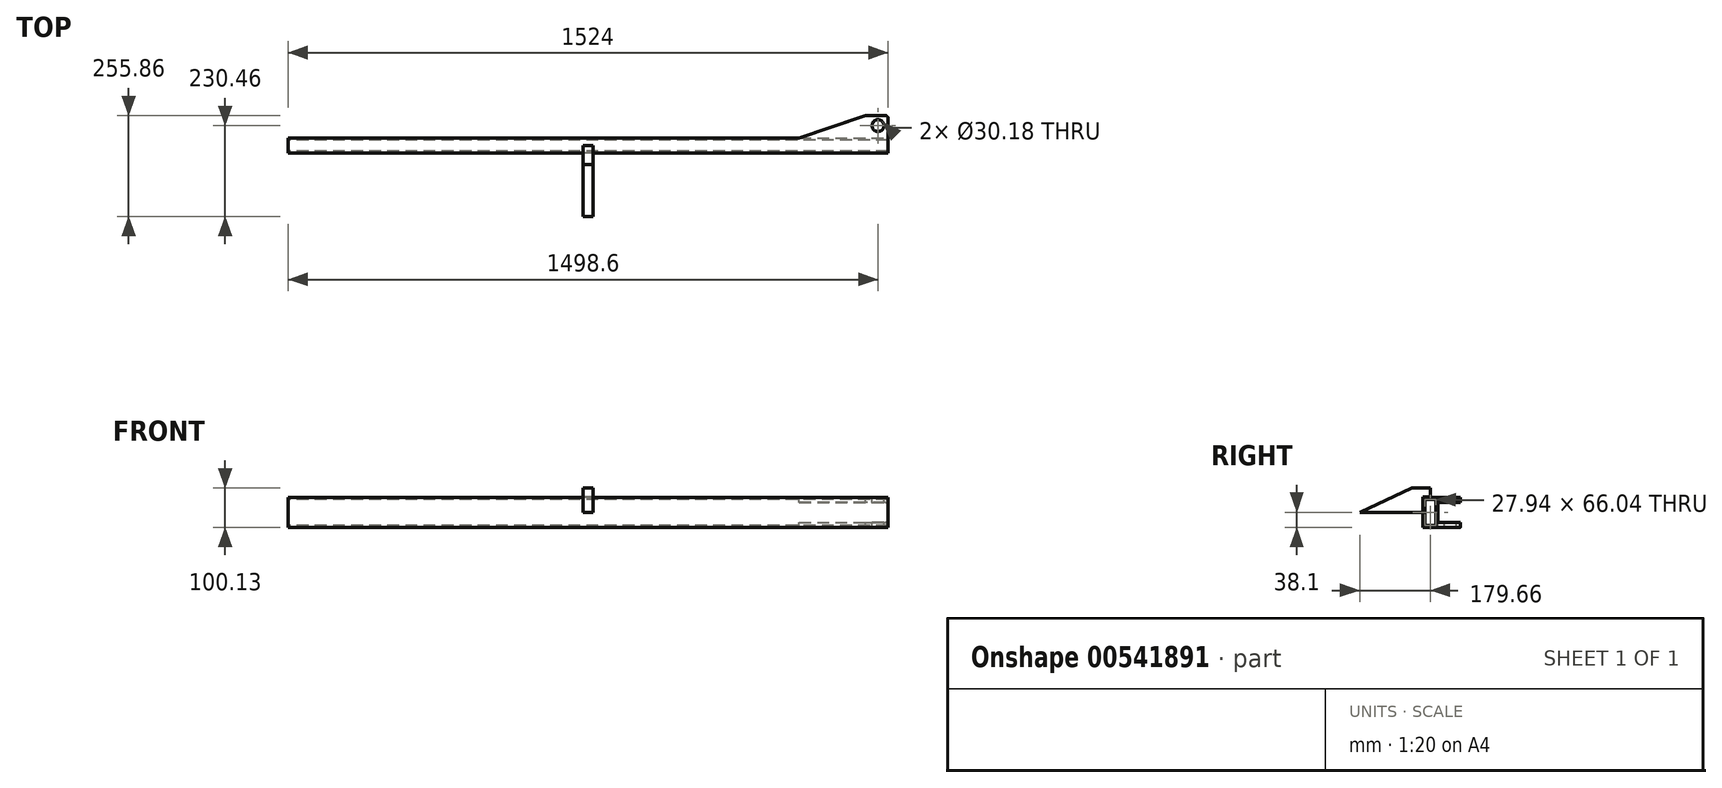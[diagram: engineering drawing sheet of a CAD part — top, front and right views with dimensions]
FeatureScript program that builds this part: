
annotation { "Feature Type Name" : "Feature", "Feature Type Description" : "" }
export const myFeature = defineFeature(function(context is Context, id is Id, definition is map)
    precondition{}
    {
        {
            var Q0;
            Q0=qCreatedBy(makeId("Right.planeOp"),FACE);
            var sketch = newSketch(context, id + "F0", { "sketchPlane" : qUnion([Q0])});
            skLineSegment(sketch, "E0.bottom", {"start": v(-19.05, 38.1) * mm, "end": v(19.05, 38.1) * mm});
            skLineSegment(sketch, "E0.top", {"start": v(-19.05, -38.1) * mm, "end": v(19.05, -38.1) * mm});
            skLineSegment(sketch, "E0.left", {"start": v(-19.05, 38.1) * mm, "end": v(-19.05, -38.1) * mm});
            skLineSegment(sketch, "E0.right", {"start": v(19.05, 38.1) * mm, "end": v(19.05, -38.1) * mm});
            skPoint(sketch, "E0.middle", {"position": v(0, 0) * mm});
            skSolve(sketch);
        }
        {
            var Q0;
            Q0 = qSketchRegion(id + "F0", true);
            extrude(context, id + "F1", {"entities" : qUnion([Q0]), "endBound" : BoundingType.SYMMETRIC, "depth" : 1524 * mm, "offsetDistance" : 25.4 * mm});
        }
        {
            var Q0;
            Q0=makeQuery(id+"F1.opExtrude","CAP_FACE",FACE,{"disambiguationData":[OSD([sQuery(id+"F0.wireOp",EDGE,"E0.bottom"),sQuery(id+"F0.wireOp",EDGE,"E0.top"),sQuery(id+"F0.wireOp",EDGE,"E0.left"),sQuery(id+"F0.wireOp",EDGE,"E0.right")])],"isStart":true});
            var Q1;
            Q1=makeQuery(id+"F1.opExtrude","CAP_FACE",FACE,{"disambiguationData":[OSD([sQuery(id+"F0.wireOp",EDGE,"E0.bottom"),sQuery(id+"F0.wireOp",EDGE,"E0.top"),sQuery(id+"F0.wireOp",EDGE,"E0.left"),sQuery(id+"F0.wireOp",EDGE,"E0.right")])],"isStart":false});
            shell(context, id + "F2", {"entities" : qUnion([Q0, Q1]), "thickness" : 5.08 * mm});
        }
        {
            var Q0;
            Q0=makeQuery(id+"F1.opExtrude","SWEPT_FACE",FACE,{"disambiguationData":[OSD([sQuery(id+"F0.wireOp",EDGE,"E0.bottom")])]});
            var sketch = newSketch(context, id + "F3", { "sketchPlane" : qUnion([Q0])});
            skLineSegment(sketch, "E1", {"start": v(762, 19.05) * mm, "end": v(762, 69.85) * mm});
            skLineSegment(sketch, "E2", {"start": v(755.65, 76.2) * mm, "end": v(704.85, 76.2) * mm});
            skLineSegment(sketch, "E3", {"start": v(704.85, 76.2) * mm, "end": v(536.49, 19.05) * mm});
            skLineSegment(sketch, "E4", {"start": v(536.49, 19.05) * mm, "end": v(762, 19.05) * mm});
            skPoint(sketch, "E5.visualSharp", {"position": v(762, 76.2) * mm});
            skArc(sketch, "E5.filletArc", {"start": v(762, 69.85) * mm, "mid": v(760.14, 74.34) * mm, "end": v(755.65, 76.2) * mm});
            skCircle(sketch, "E6", {"center": v(736.6, 50.8) * mm, "radius": 15.09 * mm});
            skSolve(sketch);
        }
        {
            var Q0;
            Q0 = qSketchRegion(id + "F3", true);
            extrude(context, id + "F4", {"entities" : qUnion([Q0]), "operationType" : NewBodyOperationType.ADD, "oppositeDirection" : true, "depth" : 76.2 * mm, "offsetDistance" : 25.4 * mm});
        }
        {
            var Q0;
            Q0=makeQuery(id+"F4.boolean.opBoolean","MERGE",FACE,{"derivedFrom":[makeQuery(id+"F1.opExtrude","CAP_FACE",FACE,{"disambiguationData":[OSD([sQuery(id+"F0.wireOp",EDGE,"E0.bottom"),sQuery(id+"F0.wireOp",EDGE,"E0.top"),sQuery(id+"F0.wireOp",EDGE,"E0.left"),sQuery(id+"F0.wireOp",EDGE,"E0.right")])],"isStart":false}),makeQuery(id+"F4.opExtrude","SWEPT_FACE",FACE,{"disambiguationData":[OSD([sQuery(id+"F3.wireOp",EDGE,"E1")])]})]});
            var sketch = newSketch(context, id + "F5", { "sketchPlane" : qUnion([Q0])});
            skLineSegment(sketch, "E7.bottom", {"start": v(69.85, 25.4) * mm, "end": v(19.05, 25.4) * mm});
            skLineSegment(sketch, "E7.top", {"start": v(69.85, -25.4) * mm, "end": v(19.05, -25.4) * mm});
            skLineSegment(sketch, "E7.right", {"start": v(19.05, 25.4) * mm, "end": v(19.05, -25.4) * mm});
            skLineSegment(sketch, "E8", {"start": v(69.85, 25.4) * mm, "end": v(77.08, 25.4) * mm});
            skLineSegment(sketch, "E9", {"start": v(77.08, 25.4) * mm, "end": v(77.08, -25.41) * mm});
            skLineSegment(sketch, "E10", {"start": v(77.08, -25.41) * mm, "end": v(69.85, -25.4) * mm});
            skSolve(sketch);
        }
        {
            var Q0;
            Q0 = qSketchRegion(id + "F5", true);
            extrude(context, id + "F6", {"entities" : qUnion([Q0]), "operationType" : NewBodyOperationType.REMOVE, "endBound" : BoundingType.THROUGH_ALL, "oppositeDirection" : true, "depth" : 25.4 * mm, "offsetDistance" : 25.4 * mm});
        }
        {
            var Q0;
            Q0=qCreatedBy(makeId("Right.planeOp"),FACE);
            var sketch = newSketch(context, id + "F7", { "sketchPlane" : qUnion([Q0])});
            skLineSegment(sketch, "E11", {"start": v(0, 38.7) * mm, "end": v(0, 62.03) * mm});
            skLineSegment(sketch, "E12", {"start": v(0, 62.03) * mm, "end": v(-47.53, 62.03) * mm});
            skLineSegment(sketch, "E13", {"start": v(-47.53, 62.03) * mm, "end": v(-179.66, 0) * mm});
            skLineSegment(sketch, "E14", {"start": v(-179.66, 0) * mm, "end": v(-19.05, 0) * mm});
            skLineSegment(sketch, "E15", {"start": v(-19.05, 0) * mm, "end": v(-19.05, 38.7) * mm});
            skLineSegment(sketch, "E16", {"start": v(-19.05, 38.7) * mm, "end": v(0, 38.7) * mm});
            skSolve(sketch);
        }
        {
            var Q0;
            Q0 = qSketchRegion(id + "F7", true);
            extrude(context, id + "F8", {"entities" : qUnion([Q0]), "endBound" : BoundingType.SYMMETRIC, "depth" : 25.4 * mm, "offsetDistance" : 25.4 * mm});
        }
    });
